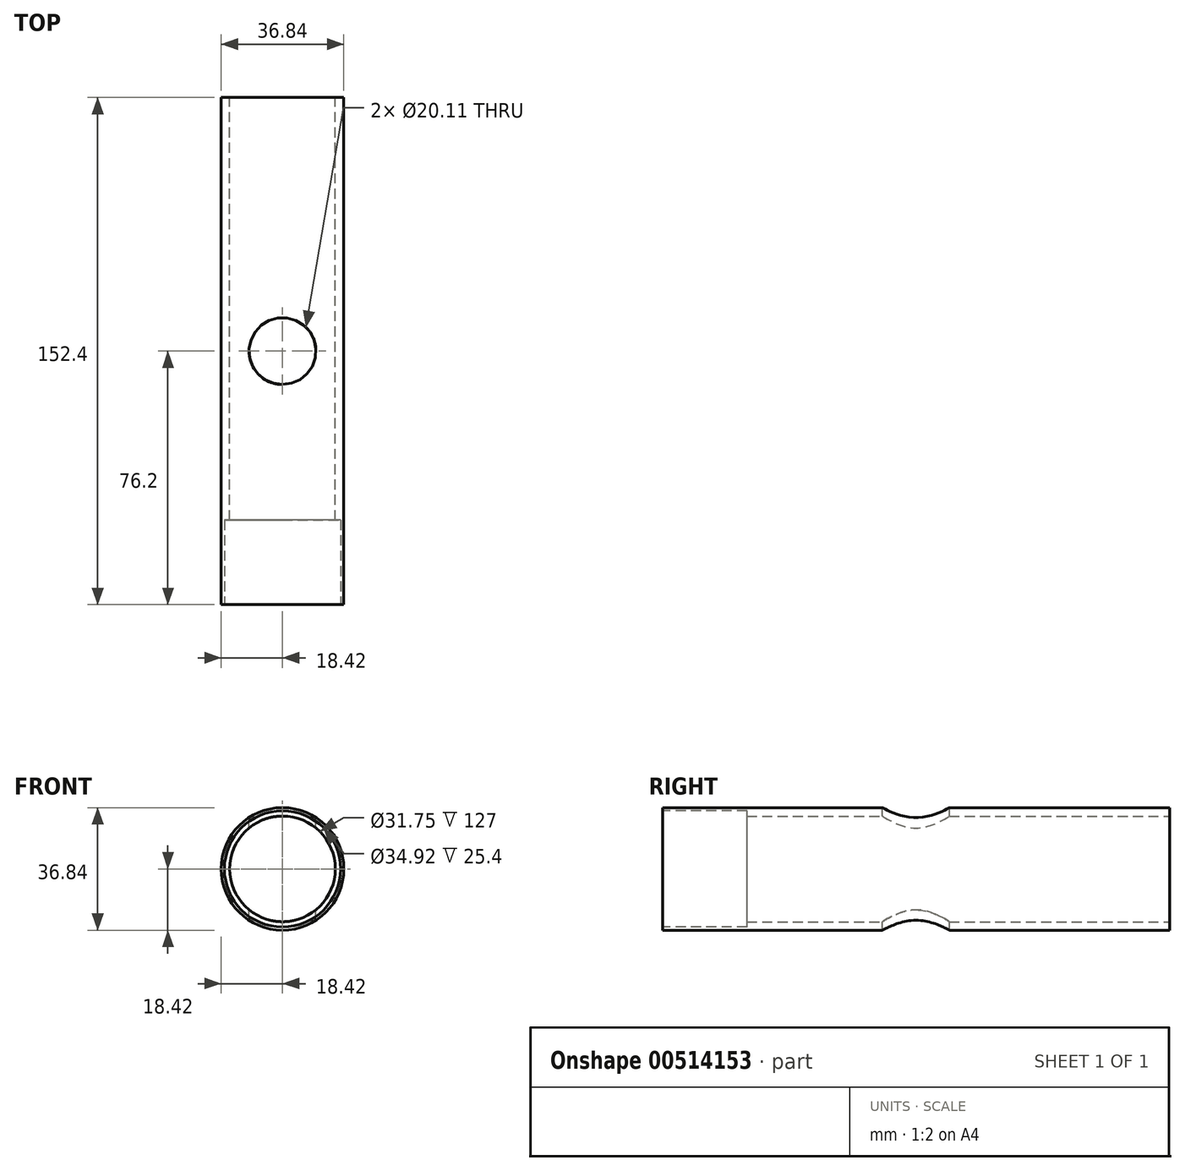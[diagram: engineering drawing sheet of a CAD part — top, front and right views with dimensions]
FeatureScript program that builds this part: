
annotation { "Feature Type Name" : "Feature", "Feature Type Description" : "" }
export const myFeature = defineFeature(function(context is Context, id is Id, definition is map)
    precondition{}
    {
        {
            var Q0;
            Q0=qCreatedBy(makeId("Front.planeOp"),FACE);
            var sketch = newSketch(context, id + "F0", { "sketchPlane" : qUnion([Q0])});
            skCircle(sketch, "E0", {"center": v(0, 0) * mm, "radius": 18.41 * mm});
            skCircle(sketch, "E1", {"center": v(0, 0) * mm, "radius": 15.88 * mm});
            skSolve(sketch);
        }
        {
            var Q0;
            Q0=makeQuery(id+"F0.imprint","IMPRINT",FACE,{"disambiguationData":[TD([[makeQuery(id+"F0.imprint","IMPRINT",EDGE,{"derivedFrom":sQuery(id+"F0.wireOp",EDGE,"E0")}),1.0]])]});
            extrude(context, id + "F1", {"entities" : qUnion([Q0]), "endBound" : BoundingType.SYMMETRIC, "depth" : 152.4 * mm});
        }
        {
            var Q0;
            Q0=qCreatedBy(makeId("Top.planeOp"),FACE);
            var sketch = newSketch(context, id + "F2", { "sketchPlane" : qUnion([Q0])});
            skCircle(sketch, "E2", {"center": v(0, 0) * mm, "radius": 10.05 * mm});
            skSolve(sketch);
        }
        {
            var Q0;
            Q0 = qSketchRegion(id + "F2", true);
            extrude(context, id + "F3", {"entities" : qUnion([Q0]), "operationType" : NewBodyOperationType.REMOVE, "endBound" : BoundingType.SYMMETRIC, "oppositeDirection" : true, "depth" : 81.28 * mm});
        }
        {
            var Q0;
            Q0=qCreatedBy(makeId("Top.planeOp"),FACE);
            var sketch = newSketch(context, id + "F4", { "sketchPlane" : qUnion([Q0])});
            skLineSegment(sketch, "E3.bottom", {"start": v(-16.64, -62.21) * mm, "end": v(-19.8, -62.21) * mm});
            skLineSegment(sketch, "E3.top", {"start": v(-16.64, -56.24) * mm, "end": v(-19.8, -56.24) * mm});
            skLineSegment(sketch, "E3.left", {"start": v(-16.64, -62.21) * mm, "end": v(-16.64, -56.24) * mm});
            skLineSegment(sketch, "E3.right", {"start": v(-19.8, -62.21) * mm, "end": v(-19.8, -56.24) * mm});
            skSolve(sketch);
        }
        {
            var Q0;
            Q0=makeQuery(id+"F1.opExtrude","CAP_FACE",FACE,{"disambiguationData":[OSD([sQuery(id+"F0.wireOp",EDGE,"E0"),sQuery(id+"F0.wireOp",EDGE,"E1")])],"isStart":false});
            var sketch = newSketch(context, id + "F5", { "sketchPlane" : qUnion([Q0])});
            skCircle(sketch, "E4", {"center": v(0, 0) * mm, "radius": 17.46 * mm});
            skSolve(sketch);
        }
        {
            var Q0;
            Q0 = qSketchRegion(id + "F5", true);
            extrude(context, id + "F6", {"entities" : qUnion([Q0]), "operationType" : NewBodyOperationType.REMOVE, "oppositeDirection" : true, "depth" : 25.4 * mm});
        }
    });
